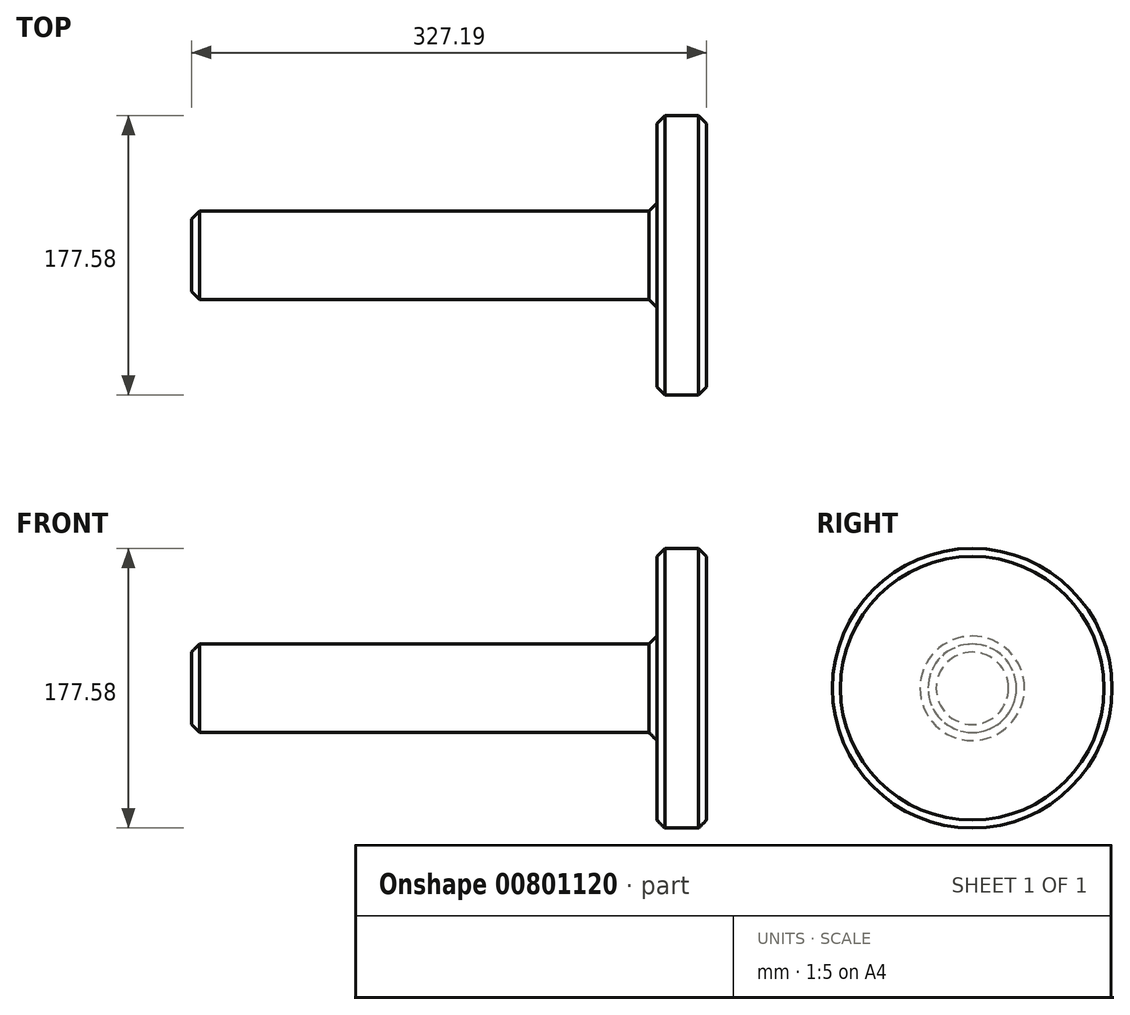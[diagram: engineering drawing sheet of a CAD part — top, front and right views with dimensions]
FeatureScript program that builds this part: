
annotation { "Feature Type Name" : "Feature", "Feature Type Description" : "" }
export const myFeature = defineFeature(function(context is Context, id is Id, definition is map)
    precondition{}
    {
        {
            var Q0;
            Q0=qCreatedBy(makeId("Right.planeOp"),FACE);
            var sketch = newSketch(context, id + "F0", { "sketchPlane" : qUnion([Q0])});
            skCircle(sketch, "E0", {"center": v(0, 0) * mm, "radius": 88.79 * mm});
            skSolve(sketch);
        }
        {
            var Q0;
            Q0=makeQuery(id+"F0.imprint","IMPRINT",FACE,{"disambiguationData":[TD([[makeQuery(id+"F0.imprint","IMPRINT",EDGE,{"derivedFrom":sQuery(id+"F0.wireOp",EDGE,"E0")}),1.0]])]});
            extrude(context, id + "F1", {"entities" : qUnion([Q0]), "depth" : 31.55 * mm, "offsetDistance" : 25.4 * mm});
        }
        {
            var Q0;
            Q0=makeQuery(id+"F1.opExtrude","CAP_FACE",FACE,{"disambiguationData":[OSD([sQuery(id+"F0.wireOp",EDGE,"E0")])],"isStart":true});
            var sketch = newSketch(context, id + "F2", { "sketchPlane" : qUnion([Q0])});
            skCircle(sketch, "E1", {"center": v(0, 0) * mm, "radius": 28.07 * mm});
            skSolve(sketch);
        }
        {
            var Q0;
            Q0 = qSketchRegion(id + "F2", true);
            extrude(context, id + "F3", {"entities" : qUnion([Q0]), "operationType" : NewBodyOperationType.ADD, "depth" : 295.64 * mm, "offsetDistance" : 25.4 * mm});
        }
        {
            var Q0;
            Q0=makeQuery(id+"F3.opExtrude","SWEPT_FACE",FACE,{"disambiguationData":[OSD([sQuery(id+"F2.wireOp",EDGE,"E1")])]});
            var Q1;
            Q1=makeQuery(id+"F3.opExtrude","CAP_EDGE",EDGE,{"disambiguationData":[OSD([sQuery(id+"F2.wireOp",EDGE,"E1")])],"isStart":true});
            chamfer(context, id + "F4", {"entities" : qUnion([Q0, Q1]), "width" : 5.08 * mm, "tangentPropagation" : true});
        }
        {
            var Q0;
            Q0=makeQuery(id+"F1.opExtrude","CAP_EDGE",EDGE,{"disambiguationData":[OSD([sQuery(id+"F0.wireOp",EDGE,"E0")])],"isStart":false});
            var Q1;
            Q1=makeQuery(id+"F1.opExtrude","CAP_EDGE",EDGE,{"disambiguationData":[OSD([sQuery(id+"F0.wireOp",EDGE,"E0")])],"isStart":true});
            chamfer(context, id + "F5", {"entities" : qUnion([Q0, Q1]), "width" : 5.08 * mm, "tangentPropagation" : true});
        }
        {
            var Q0;
            Q0=makeQuery(id+"F1.opExtrude","CAP_FACE",FACE,{"disambiguationData":[OSD([sQuery(id+"F0.wireOp",EDGE,"E0")])],"isStart":false});
            var sketch = newSketch(context, id + "F6", { "sketchPlane" : qUnion([Q0])});
            skSolve(sketch);
        }
    });
